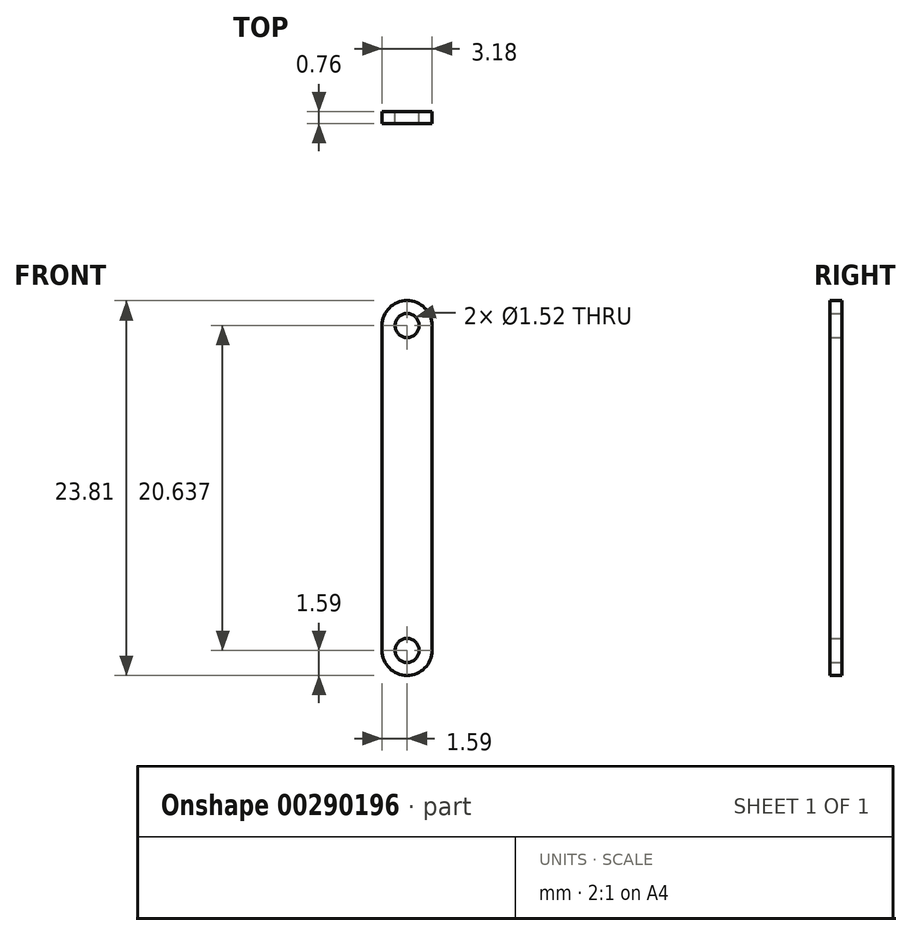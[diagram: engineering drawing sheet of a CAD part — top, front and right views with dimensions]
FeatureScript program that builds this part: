
annotation { "Feature Type Name" : "Feature", "Feature Type Description" : "" }
export const myFeature = defineFeature(function(context is Context, id is Id, definition is map)
    precondition{}
    {
        {
            var Q0;
            Q0=qCreatedBy(makeId("Front.planeOp"),FACE);
            var sketch = newSketch(context, id + "F0", { "sketchPlane" : qUnion([Q0])});
            skLineSegment(sketch, "E0", {"start": v(0, 0) * mm, "end": v(0, 20.64) * mm, "construction": true});
            skArc(sketch, "E1.0.startCap", {"start": v(1.59, 0) * mm, "mid": v(0, -1.59) * mm, "end": v(-1.59, 0) * mm});
            skArc(sketch, "E1.0.endCap", {"start": v(-1.59, 20.64) * mm, "mid": v(0, 22.23) * mm, "end": v(1.59, 20.64) * mm});
            skLineSegment(sketch, "E1.0.left", {"start": v(-1.59, 0) * mm, "end": v(-1.59, 20.64) * mm});
            skLineSegment(sketch, "E1.0.right", {"start": v(1.59, 0) * mm, "end": v(1.59, 20.64) * mm});
            skCircle(sketch, "E2", {"center": v(0, 0) * mm, "radius": 0.76 * mm});
            skCircle(sketch, "E3", {"center": v(0, 20.64) * mm, "radius": 0.76 * mm});
            skSolve(sketch);
        }
        {
            var Q0;
            Q0 = qSketchRegion(id + "F0", true);
            extrude(context, id + "F1", {"entities" : qUnion([Q0]), "endBound" : BoundingType.SYMMETRIC, "depth" : 0.76 * mm});
        }
    });
